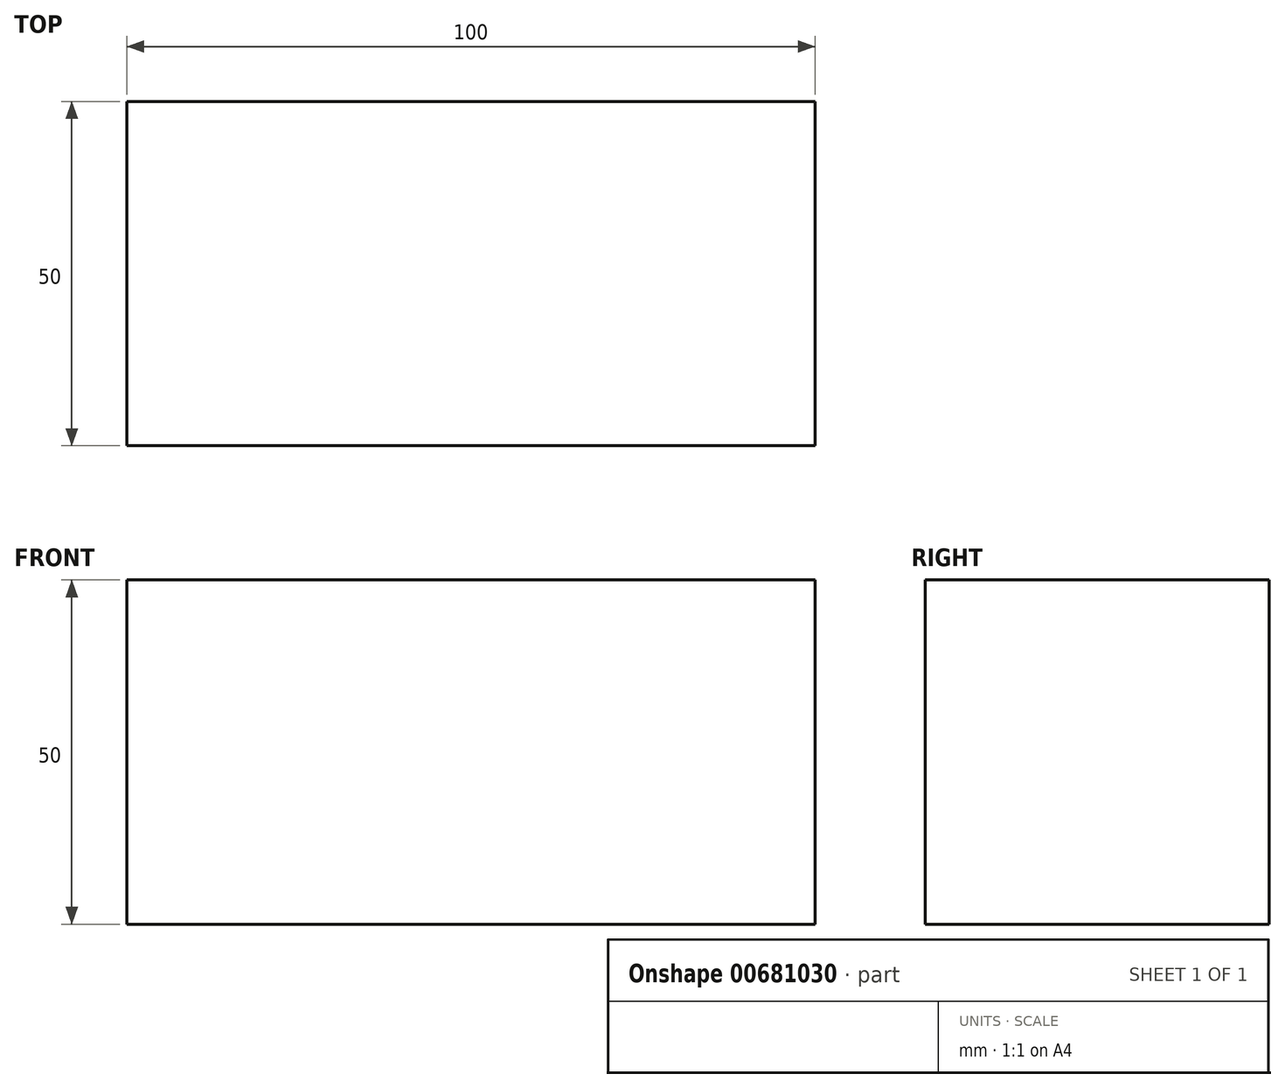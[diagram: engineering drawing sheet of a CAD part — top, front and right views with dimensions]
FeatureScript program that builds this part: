
annotation { "Feature Type Name" : "Feature", "Feature Type Description" : "" }
export const myFeature = defineFeature(function(context is Context, id is Id, definition is map)
    precondition{}
    {
        {
            var Q0;
            Q0=qCreatedBy(makeId("Top.planeOp"),FACE);
            var sketch = newSketch(context, id + "F0", { "sketchPlane" : qUnion([Q0])});
            skLineSegment(sketch, "E0.bottom", {"start": v(0, 0) * mm, "end": v(100, 0) * mm});
            skLineSegment(sketch, "E0.top", {"start": v(0, 50) * mm, "end": v(100, 50) * mm});
            skLineSegment(sketch, "E0.left", {"start": v(0, 0) * mm, "end": v(0, 50) * mm});
            skLineSegment(sketch, "E0.right", {"start": v(100, 0) * mm, "end": v(100, 50) * mm});
            skSolve(sketch);
        }
        {
            var Q0;
            Q0 = qSketchRegion(id + "F0", true);
            extrude(context, id + "F1", {"entities" : qUnion([Q0]), "depth" : 50 * mm, "offsetDistance" : 25 * mm});
        }
    });
